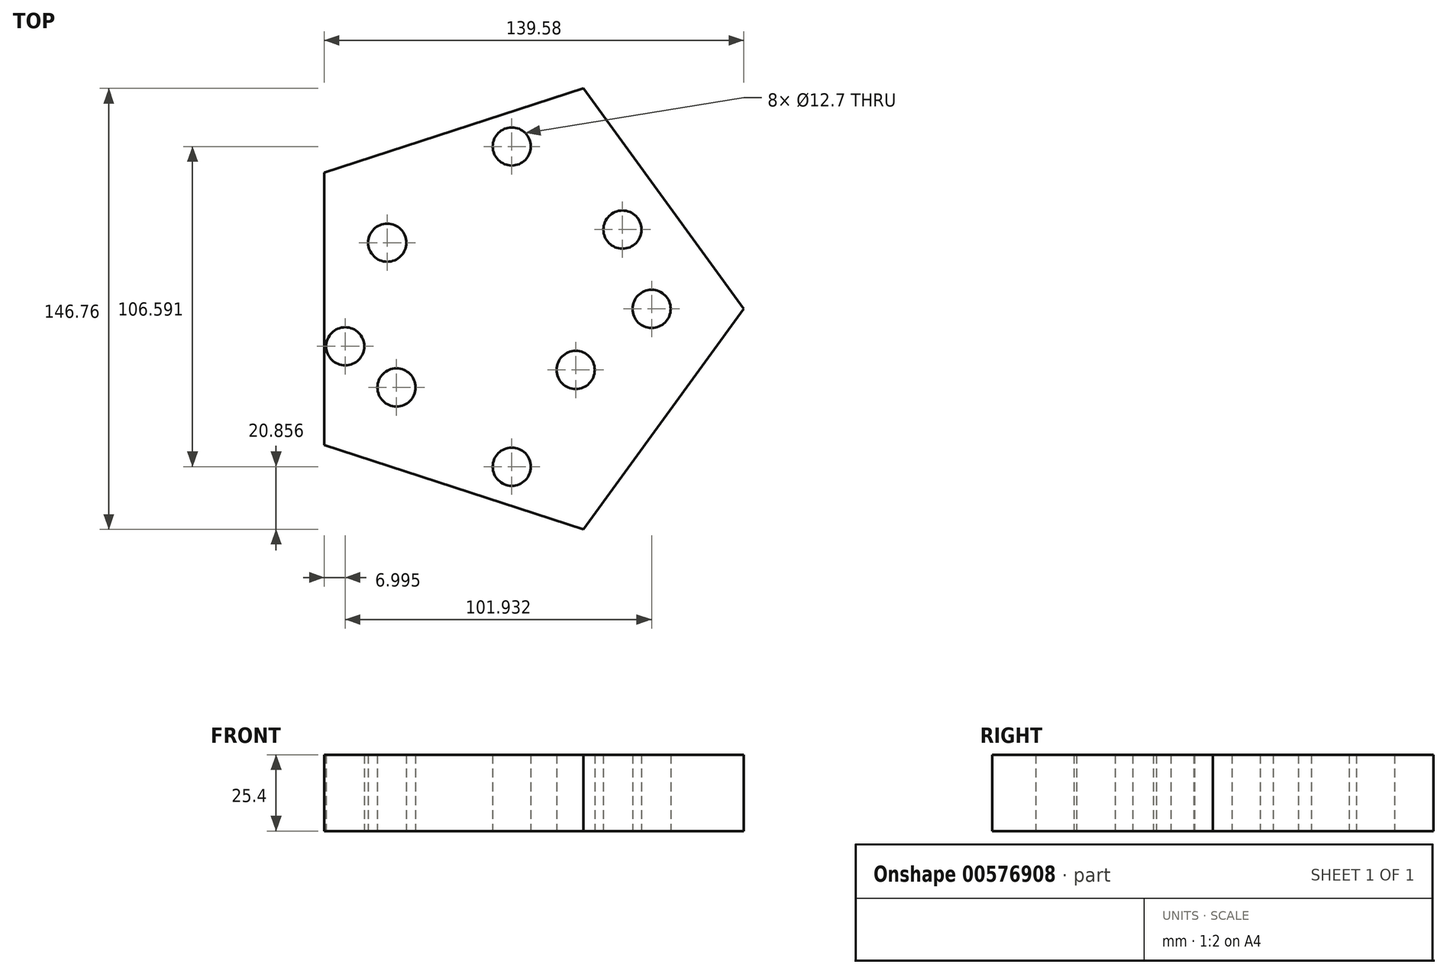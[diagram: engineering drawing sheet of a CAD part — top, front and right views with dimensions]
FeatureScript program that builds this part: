
annotation { "Feature Type Name" : "Feature", "Feature Type Description" : "" }
export const myFeature = defineFeature(function(context is Context, id is Id, definition is map)
    precondition{}
    {
        {
            var Q0;
            Q0=qCreatedBy(makeId("Top.planeOp"),FACE);
            var sketch = newSketch(context, id + "F0", { "sketchPlane" : qUnion([Q0])});
            skCircle(sketch, "E0.cCircle", {"center": v(0, 0) * mm, "radius": 77.16 * mm, "construction": true});
            skLineSegment(sketch, "E0.0", {"start": v(77.16, 0) * mm, "end": v(23.84, -73.38) * mm});
            skLineSegment(sketch, "E0.1", {"start": v(23.84, -73.38) * mm, "end": v(-62.42, -45.35) * mm});
            skLineSegment(sketch, "E0.2", {"start": v(-62.42, -45.35) * mm, "end": v(-62.42, 45.35) * mm});
            skLineSegment(sketch, "E0.3", {"start": v(-62.42, 45.35) * mm, "end": v(23.84, 73.38) * mm});
            skLineSegment(sketch, "E0.4", {"start": v(23.84, 73.38) * mm, "end": v(77.16, 0) * mm});
            skSolve(sketch);
        }
        {
            var Q0;
            Q0=makeQuery(id+"F0.imprint","IMPRINT",FACE,{"disambiguationData":[TD([[makeQuery(id+"F0.imprint","IMPRINT",EDGE,{"derivedFrom":sQuery(id+"F0.wireOp",EDGE,"E0.0")}),-1.0]])]});
            extrude(context, id + "F1", {"entities" : qUnion([Q0]), "depth" : 25.4 * mm, "offsetDistance" : 25.4 * mm});
        }
        {
            var Q0;
            Q0=qCreatedBy(makeId("Top.planeOp"),FACE);
            var sketch = newSketch(context, id + "F2", { "sketchPlane" : qUnion([Q0])});
            skPoint(sketch, "E1", {"position": v(46.5, 0) * mm});
            skPoint(sketch, "E2", {"position": v(0, -52.52) * mm});
            skPoint(sketch, "E3", {"position": v(-55.42, -12.46) * mm});
            skPoint(sketch, "E4", {"position": v(0, 54.07) * mm});
            skPoint(sketch, "E5", {"position": v(-41.44, 22.04) * mm});
            skPoint(sketch, "E6", {"position": v(21.25, -20.3) * mm});
            skPoint(sketch, "E7", {"position": v(-38.36, -26.14) * mm});
            skPoint(sketch, "E8", {"position": v(36.82, 26.39) * mm});
            skSolve(sketch);
        }
        {
            var Q0;
            Q0=sQuery(id+"F2.wireOp",VERTEX,"E7");
            var Q1;
            Q1=sQuery(id+"F2.wireOp",VERTEX,"E2");
            var Q2;
            Q2=sQuery(id+"F2.wireOp",VERTEX,"E6");
            var Q3;
            Q3=sQuery(id+"F2.wireOp",VERTEX,"E1");
            var Q4;
            Q4=sQuery(id+"F2.wireOp",VERTEX,"E8");
            var Q5;
            Q5=sQuery(id+"F2.wireOp",VERTEX,"E3");
            var Q6;
            Q6=sQuery(id+"F2.wireOp",VERTEX,"E5");
            var Q7;
            Q7=sQuery(id+"F2.wireOp",VERTEX,"E4");
            var Q8;
            Q8=makeQuery(id+"F1.opExtrude","SWEPT_BODY",BODY,{"disambiguationData":[OSD([sQuery(id+"F0.wireOp",EDGE,"E0.0"),sQuery(id+"F0.wireOp",EDGE,"E0.1"),sQuery(id+"F0.wireOp",EDGE,"E0.2"),sQuery(id+"F0.wireOp",EDGE,"E0.3"),sQuery(id+"F0.wireOp",EDGE,"E0.4")])]});
            hole(context, id + "F3", {"style" : HoleStyle.SIMPLE, "endStyle" : HoleEndStyle.THROUGH, "oppositeDirection" : true, "holeDiameter" : 12.7 * mm, "isTappedThrough" : true, "tappedDepth" : 12.7 * mm, "tapClearance" : 3, "locations" : qUnion([Q0, Q1, Q2, Q3, Q4, Q5, Q6, Q7]), "scope" : qUnion([Q8])});
        }
    });
